# Revit family: IS_ConceptAir_Multiproduct_BIM_GB_E0832;E0834
name_source: partatom
category: Plumbing Fixtures
revit_build: Autodesk Revit MEP 2014 (Build: 20140709_2115(x64)
units: mm (PartAtom-declared; Revit-internal decimal feet)

## types (12) — shared parameters
Accessories = www.idealspec.co.uk
AreaUnits = millimeters
Assembly Code = C1030200
AssetType = Fixed
BREEAM = No
Brand = IdealStandard
Default Elevation = 2000 mm
DurationUnit = year
ECA = No
ExpectedLife = 30
IfcExportAs = IfcFurnitureType
IfcExportType = USERDEFINED
InstallationInstructions = www.idealspec.co.uk/resources.html
LinearUnits = millimeters
ManufacturerURL = www.idealspec.co.uk
Material = Laquered MDF
NBSDescription = Bathroom integrated duct work
NBSReference = 45-35-72/320
NettWeight = 0 Kg
NominalDepth = 300 mm
NominalLength = 300 mm
NominalWidth = 400 mm
Shape = Rectangular
Space = Internal
SpareParts = www.fastpart-spares.co.uk
TMV3 = No
URL = www.idealspec.co.uk
Uniclass2 = Pr_40_30_78_04
Version = 1
VolumeUnits = Litres
WRAS = No
WarrantyDescription = Manufacturers warranty
WarrantyDurationParts = 5
WarrantyDurationUnit = year
WaterEfficientProduct = No
zero-valued in all types: CWFU, Cost, HWFU, WFU

## per-type parameters (varying)
| type | BIMObjectName | Color | Description | Features | Finish | InnerColour | MainColor | MainColour | Model | ModelNumber | ModelReference | Name | NominalHeight | ProductInformation | Size |
| E0834B2 - 1200 Column Unit Gls White + Matt White | ISI_IdealStandard_Furniture_ConceptAir_E0834B2 | White | Concept Air 1200 Column Unit Gls White + Matt White | 1200 Column Unit Gls White + Matt White | White | ISI_IdealStandard_Laminate_White_Render | White | ISI_IdealStandard_Laminate_White_Render | E0834B2 | E0834B2 | Concept Air 1200 Column Unit Gls White + Matt White | Furniture_ConceptAir_E0834B2_IdealStandard | 1200 mm | www.idealspec.co.uk/assets/datasheet/E0834B2 | 400 x 300 x 1200 mm |
| E0834EQ - 1200 Column Unit Gls Light Grey + Matt White | ISI_IdealStandard_Furniture_ConceptAir_E0834EQ | Grey | Concept Air 1200 Column Unit Gls Light Grey + Matt White | 1200 Column Unit Gls Light Grey + Matt White | Grey | ISI_IdealStandard_Laminate_White_Render | Grey | ISI_IdealStandard_Furniture_Grey_Render | E0834EQ | E0834EQ | Concept Air 1200 Column Unit Gls Light Grey + Matt White | Furniture_ConceptAir_E0834EQ_IdealStandard | 1200 mm | www.idealspec.co.uk/assets/datasheet/E0834EQ | 400 x 300 x 1200 mm |
| E0834KN - 1200 Column Unit Gls White + Matt Light Grey | ISI_IdealStandard_Furniture_ConceptAir_E0834KN | White | Concept Air 1200 Column Unit Gls White + Matt Light Grey | 1200 Column Unit Gls White + Matt Light Grey | White | ISI_IdealStandard_Furniture_Grey_Render | White | ISI_IdealStandard_Laminate_White_Render | E0834KN | E0834KN | Concept Air 1200 Column Unit Gls White + Matt Light Grey | Furniture_ConceptAir_E0834KN_IdealStandard | 1200 mm | www.idealspec.co.uk/assets/datasheet/E0834KN | 400 x 300 x 1200 mm |
| E0834PS - 1200 Column Unit Wood Light Grey + Matt White | ISI_IdealStandard_Furniture_ConceptAir_E0834PS | Wood grey | Concept Air 1200 Column Unit Wood Light Grey + Matt White | 1200 Column Unit Wood Light Grey + Matt White | Wood grey | ISI_IdealStandard_Laminate_White_Render | Wood grey | ISI_IdealStandard_Furniture_WoodLightGrey_Render | E0834PS | E0834PS | Concept Air 1200 Column Unit Wood Light Grey + Matt White | Furniture_ConceptAir_E0834PS_IdealStandard | 1200 mm | www.idealspec.co.uk/assets/datasheet/E0834PS | 400 x 300 x 1200 mm |
| E0834UK - 1200 Column Unit Wood Light Brown + Matt Light Brown | ISI_IdealStandard_Furniture_ConceptAir_E0834UK | Wood brown | Concept Air 1200 Column Unit Wood Light Brown + Matt Light Brown | 1200 Column Unit Wood Light Brown + Matt Light Brown | Wood brown | ISI_IdealStandard_Furniture_WoodLightBrown_Render | Wood brown | ISI_IdealStandard_Furniture_WoodLightBrown_Render | E0834UK | E0834UK | Concept Air 1200 Column Unit Wood Light Brown + Matt Light Brown | Furniture_ConceptAir_E0834UK_IdealStandard | 1200 mm | www.idealspec.co.uk/assets/datasheet/E0834UK | 400 x 300 x 1200 mm |
| E0832B2 - 1600 Column Unit Gls White + Matt White | ISI_IdealStandard_Furniture_ConceptAir_E0832B2 | White | Concept Air 1600 Column Unit Gls White + Matt White | 1600 Column Unit Gls White + Matt White | White | ISI_IdealStandard_Laminate_White_Render | White | ISI_IdealStandard_Laminate_White_Render | E0832B2 | E0832B2 | Concept Air 1600 Column Unit Gls White + Matt White | Furniture_ConceptAir_E0832B2_IdealStandard | 1600 mm | www.idealspec.co.uk/assets/datasheet/E0832B2 | 400 x 300 x 1600 mm |
| E0832EQ - 1600 Column Unit Gls Light Grey + Matt White | ISI_IdealStandard_Furniture_ConceptAir_E0832EQ | Grey | Concept Air 1600 Column Unit Gls Light Grey + Matt White | 1600 Column Unit Gls Light Grey + Matt White | Grey | ISI_IdealStandard_Laminate_White_Render | Grey | ISI_IdealStandard_Furniture_Grey_Render | E0832EQ | E0832EQ | Concept Air 1600 Column Unit Gls Light Grey + Matt White | Furniture_ConceptAir_E0832EQ_IdealStandard | 1600 mm | www.idealspec.co.uk/assets/datasheet/E0832EQ | 400 x 300 x 1600 mm |
| E0832KN - 1600 Column Unit Gls White + Matt Light Grey | ISI_IdealStandard_Furniture_ConceptAir_E0832KN | White | Concept Air 1600 Column Unit Gls White + Matt Light Grey | 1600 Column Unit Gls White + Matt Light Grey | White | ISI_IdealStandard_Furniture_Grey_Render | White | ISI_IdealStandard_Laminate_White_Render | E0832KN | E0832KN | Concept Air 1600 Column Unit Gls White + Matt Light Grey | Furniture_ConceptAir_E0832KN_IdealStandard | 1600 mm | www.idealspec.co.uk/assets/datasheet/E0832KN | 400 x 300 x 1600 mm |
| E0832PS - 1600 Column Unit Wood Light Grey + Matt White | ISI_IdealStandard_Furniture_ConceptAir_E0832PS | Wood grey | Concept Air 1600 Column Unit Wood Light Grey + Matt White | 1600 Column Unit Wood Light Grey + Matt White | Wood grey | ISI_IdealStandard_Laminate_White_Render | Wood grey | ISI_IdealStandard_Furniture_WoodLightGrey_Render | E0832PS | E0832PS | Concept Air 1600 Column Unit Wood Light Grey + Matt White | Furniture_ConceptAir_E0832PS_IdealStandard | 1600 mm | www.idealspec.co.uk/assets/datasheet/E0832PS | 400 x 300 x 1600 mm |
| E0832UK - 1600 Column Unit Wood Light Brown + Matt Light Brown | ISI_IdealStandard_Furniture_ConceptAir_E0832UK | Wood brown | Concept Air 1600 Column Unit Wood Light Brown + Matt Light Brown | 1600 Column Unit Wood Light Brown + Matt Light Brown | Wood brown | ISI_IdealStandard_Furniture_WoodLightBrown_Render | Wood brown | ISI_IdealStandard_Furniture_WoodLightBrown_Render | E0832UK | E0832UK | Concept Air 1600 Column Unit Wood Light Brown + Matt Light Brown | Furniture_ConceptAir_E0832UK_IdealStandard | 1600 mm | www.idealspec.co.uk/assets/datasheet/E0832UK | 400 x 300 x 1600 mm |
| E0832VY - 1600 Column Unit Matt Dark Brown + Matt White | ISI_IdealStandard_Furniture_ConceptAir_E0832VY | Dark brown | Concept Air 1600 Column Unit Matt Dark Brown + Matt White | 1600 Column Unit Matt Dark Brown + Matt White | Dark brown | ISI_IdealStandard_Laminate_White_Render | Dark brown | ISI_IdealStandard_Furniture_DarkBrown_Render | E0832VY | E0832VY | Concept Air 1600 Column Unit Gls Dark Brown + Matt White | Furniture_ConceptAir_E0832VY_IdealStandard | 1600 mm | www.idealspec.co.uk/assets/datasheet/E0832VY | 400 x 300 x 1600 mm |
| E0834VY - 1200 Column Unit Matt Dark Brown + Matt White | ISI_IdealStandard_Furniture_ConceptAir_E0834VY | Dark brown | Concept Air 1200 Column Unit Matt Dark Brown + Matt White | 1200 Column Unit Matt Dark Brown + Matt White | Dark brown | ISI_IdealStandard_Laminate_White_Render | Dark brown | ISI_IdealStandard_Furniture_DarkBrown_Render | E0834VY | E0834VY | Concept Air 1200 Column Unit Gls Dark Brown + Matt White | Furniture_ConceptAir_E0834VY_IdealStandard | 1200 mm | www.idealspec.co.uk/assets/datasheet/E0834VY | 400 x 300 x 1200 mm |

## geometry (parser evidence)
native form markers: Sweep x3
no freeform markers — native parametric forms only
